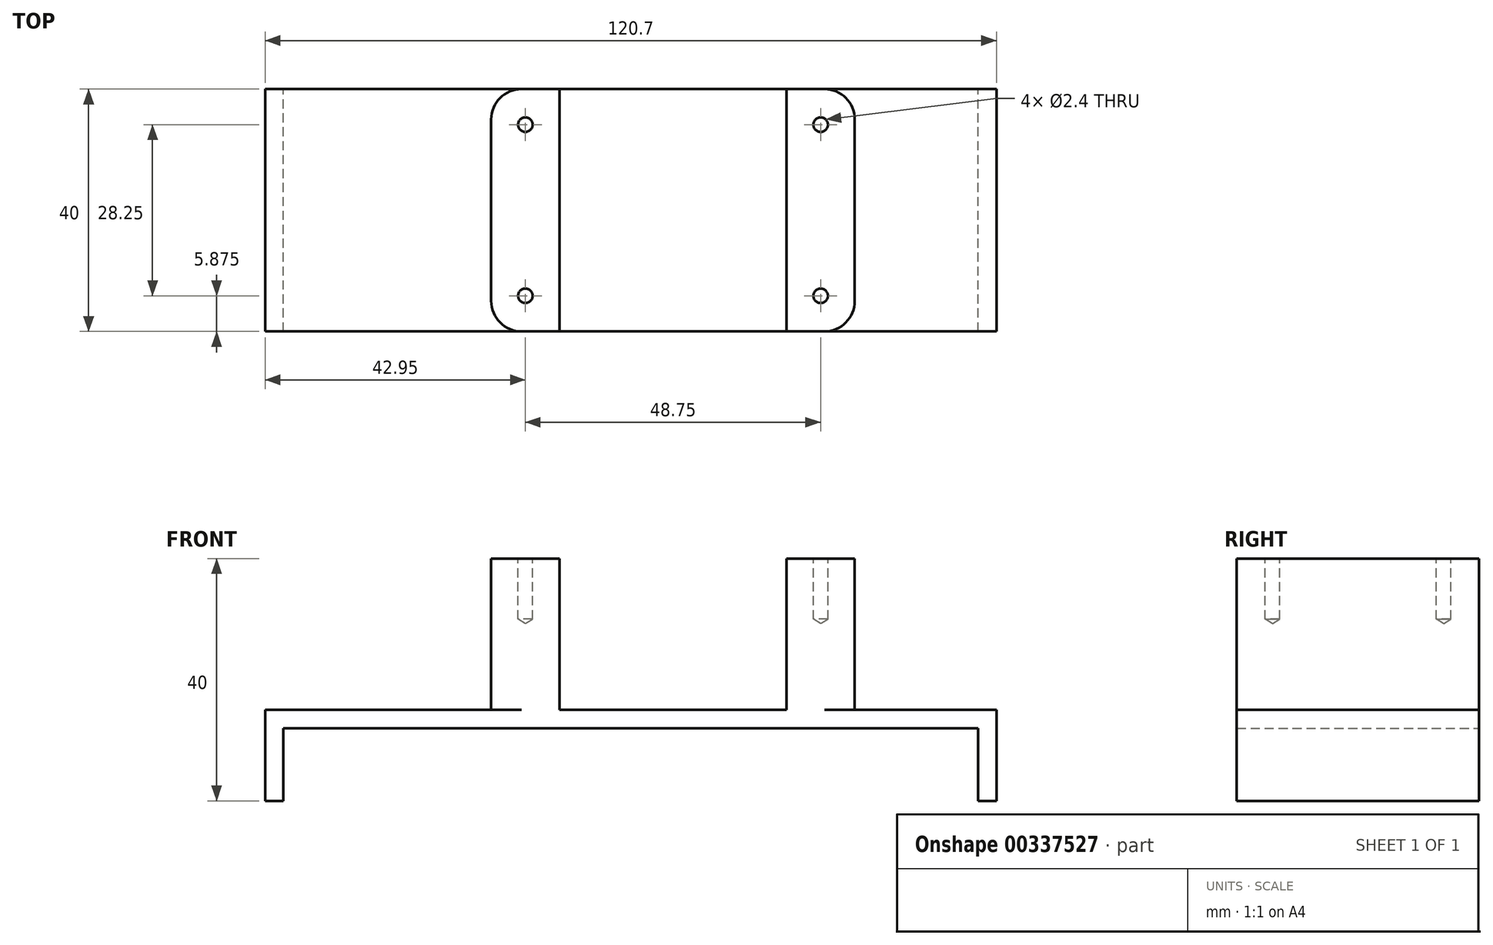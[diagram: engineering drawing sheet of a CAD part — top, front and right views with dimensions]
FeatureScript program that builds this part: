
annotation { "Feature Type Name" : "Feature", "Feature Type Description" : "" }
export const myFeature = defineFeature(function(context is Context, id is Id, definition is map)
    precondition{}
    {
        {
            var Q0;
            Q0=qCreatedBy(makeId("Front.planeOp"),FACE);
            var sketch = newSketch(context, id + "F0", { "sketchPlane" : qUnion([Q0])});
            skLineSegment(sketch, "E0.bottom", {"start": v(-60.35, 15) * mm, "end": v(60.35, 15) * mm});
            skLineSegment(sketch, "E0.top", {"start": v(-60.35, 0) * mm, "end": v(-57.35, 0) * mm});
            skLineSegment(sketch, "E0.left", {"start": v(-60.35, 15) * mm, "end": v(-60.35, 0) * mm});
            skLineSegment(sketch, "E0.right", {"start": v(60.35, 15) * mm, "end": v(60.35, 0) * mm});
            skLineSegment(sketch, "E1.top", {"start": v(-57.35, 12) * mm, "end": v(57.35, 12) * mm});
            skLineSegment(sketch, "E1.left", {"start": v(-57.35, 0) * mm, "end": v(-57.35, 12) * mm});
            skLineSegment(sketch, "E1.right", {"start": v(57.35, 0) * mm, "end": v(57.35, 12) * mm});
            skLineSegment(sketch, "E2", {"start": v(0, 0) * mm, "end": v(0, 84.45) * mm, "construction": true});
            skLineSegment(sketch, "E3.trimOffspring", {"start": v(57.35, 0) * mm, "end": v(60.35, 0) * mm});
            skSolve(sketch);
        }
        {
            var Q0;
            Q0 = qSketchRegion(id + "F0", true);
            extrude(context, id + "F1", {"entities" : qUnion([Q0]), "depth" : 40 * mm});
        }
        {
            var Q0;
            Q0=makeQuery(id+"F1.opExtrude","SWEPT_FACE",FACE,{"disambiguationData":[OSD([sQuery(id+"F0.wireOp",EDGE,"E0.bottom")])]});
            var sketch = newSketch(context, id + "F2", { "sketchPlane" : qUnion([Q0])});
            skLineSegment(sketch, "E4.bottom", {"start": v(-23.03, 0) * mm, "end": v(-11.77, 0) * mm});
            skLineSegment(sketch, "E4.top", {"start": v(-23.03, -40) * mm, "end": v(-11.77, -40) * mm});
            skLineSegment(sketch, "E4.left", {"start": v(-23.03, 0) * mm, "end": v(-23.03, -40) * mm});
            skLineSegment(sketch, "E4.right", {"start": v(36.97, 0) * mm, "end": v(36.97, -40) * mm});
            skLineSegment(sketch, "E5.bottom", {"start": v(-17.4, -5.88) * mm, "end": v(31.35, -5.88) * mm, "construction": true});
            skLineSegment(sketch, "E5.top", {"start": v(-17.4, -34.12) * mm, "end": v(31.35, -34.12) * mm, "construction": true});
            skLineSegment(sketch, "E5.left", {"start": v(-17.4, -5.87) * mm, "end": v(-17.4, -34.12) * mm, "construction": true});
            skLineSegment(sketch, "E5.right", {"start": v(31.35, -5.87) * mm, "end": v(31.35, -34.12) * mm, "construction": true});
            skLineSegment(sketch, "E6", {"start": v(-60.35, -20) * mm, "end": v(60.35, -20) * mm, "construction": true});
            skLineSegment(sketch, "E7.left", {"start": v(-11.77, 0) * mm, "end": v(-11.77, -40) * mm});
            skLineSegment(sketch, "E7.right", {"start": v(25.73, 0) * mm, "end": v(25.73, -40) * mm});
            skLineSegment(sketch, "E8.trimOffspring", {"start": v(25.73, 0) * mm, "end": v(36.97, 0) * mm});
            skLineSegment(sketch, "E9.trimOffspring", {"start": v(25.73, -40) * mm, "end": v(36.97, -40) * mm});
            skSolve(sketch);
        }
        {
            var Q0;
            Q0 = qSketchRegion(id + "F2", true);
            extrude(context, id + "F3", {"entities" : qUnion([Q0]), "operationType" : NewBodyOperationType.ADD, "depth" : 25 * mm});
        }
        {
            var Q0;
            Q0=makeQuery(id+"F3.opExtrude","CAP_FACE",FACE,{"disambiguationData":[OSD([sQuery(id+"F2.wireOp",EDGE,"E4.bottom"),sQuery(id+"F2.wireOp",EDGE,"E4.top"),sQuery(id+"F2.wireOp",EDGE,"E4.left"),sQuery(id+"F2.wireOp",EDGE,"E4.right")])],"isStart":false});
            var sketch = newSketch(context, id + "F4", { "sketchPlane" : qUnion([Q0])});
            skPoint(sketch, "E10", {"position": v(176.97, -109.06) * mm});
            skPoint(sketch, "E11.0", {"position": v(-17.4, -5.87) * mm});
            skPoint(sketch, "E11.1", {"position": v(31.35, -5.87) * mm});
            skPoint(sketch, "E11.2", {"position": v(31.35, -34.12) * mm});
            skPoint(sketch, "E11.3", {"position": v(-17.4, -34.12) * mm});
            skSolve(sketch);
        }
        {
            var Q0;
            Q0=sQuery(id+"F4.wireOp",VERTEX,"E11.0");
            var Q1;
            Q1=sQuery(id+"F4.wireOp",VERTEX,"E11.1");
            var Q2;
            Q2=sQuery(id+"F4.wireOp",VERTEX,"E11.2");
            var Q3;
            Q3=sQuery(id+"F4.wireOp",VERTEX,"E11.3");
            var Q4;
            Q4=makeQuery(id+"F1.opExtrude","SWEPT_BODY",BODY,{"disambiguationData":[OSD([sQuery(id+"F0.wireOp",EDGE,"E0.bottom"),sQuery(id+"F0.wireOp",EDGE,"E0.top"),sQuery(id+"F0.wireOp",EDGE,"E0.left"),sQuery(id+"F0.wireOp",EDGE,"E0.right"),sQuery(id+"F0.wireOp",EDGE,"E1.top"),sQuery(id+"F0.wireOp",EDGE,"E1.left"),sQuery(id+"F0.wireOp",EDGE,"E1.right"),sQuery(id+"F0.wireOp",EDGE,"E3.trimOffspring")])]});
            hole(context, id + "F5", {"style" : HoleStyle.SIMPLE, "endStyle" : HoleEndStyle.BLIND, "holeDiameter" : 2.4 * mm, "holeDepth" : 10 * mm, "tappedDepth" : 3.2 * mm, "tapClearance" : 3, "locations" : qUnion([Q0, Q1, Q2, Q3]), "scope" : qUnion([Q4])});
        }
        {
            var Q0;
            Q0=makeQuery(id+"F3.opExtrude","SWEPT_EDGE",EDGE,{"disambiguationData":[OSD([sQuery(id+"F0.wireOp",EDGE,"E0.bottom"),sQuery(id+"F2.wireOp",EDGE,"E4.bottom"),sQuery(id+"F2.wireOp",EDGE,"E4.left")])]});
            var Q1;
            Q1=makeQuery(id+"F3.opExtrude","SWEPT_EDGE",EDGE,{"disambiguationData":[OSD([sQuery(id+"F0.wireOp",EDGE,"E0.bottom"),sQuery(id+"F2.wireOp",EDGE,"E4.right"),sQuery(id+"F2.wireOp",EDGE,"E8.trimOffspring")])]});
            var Q2;
            Q2=makeQuery(id+"F3.opExtrude","SWEPT_EDGE",EDGE,{"disambiguationData":[OSD([sQuery(id+"F0.wireOp",EDGE,"E0.bottom"),sQuery(id+"F2.wireOp",EDGE,"E4.right"),sQuery(id+"F2.wireOp",EDGE,"E9.trimOffspring")])]});
            var Q3;
            Q3=makeQuery(id+"F3.opExtrude","SWEPT_EDGE",EDGE,{"disambiguationData":[OSD([sQuery(id+"F0.wireOp",EDGE,"E0.bottom"),sQuery(id+"F2.wireOp",EDGE,"E4.top"),sQuery(id+"F2.wireOp",EDGE,"E4.left")])]});
            fillet(context, id + "F6", {"entities" : qUnion([Q0, Q1, Q2, Q3]), "radius" : 5 * mm, "tangentPropagation" : true, "allowEdgeOverflow" : false});
        }
    });
